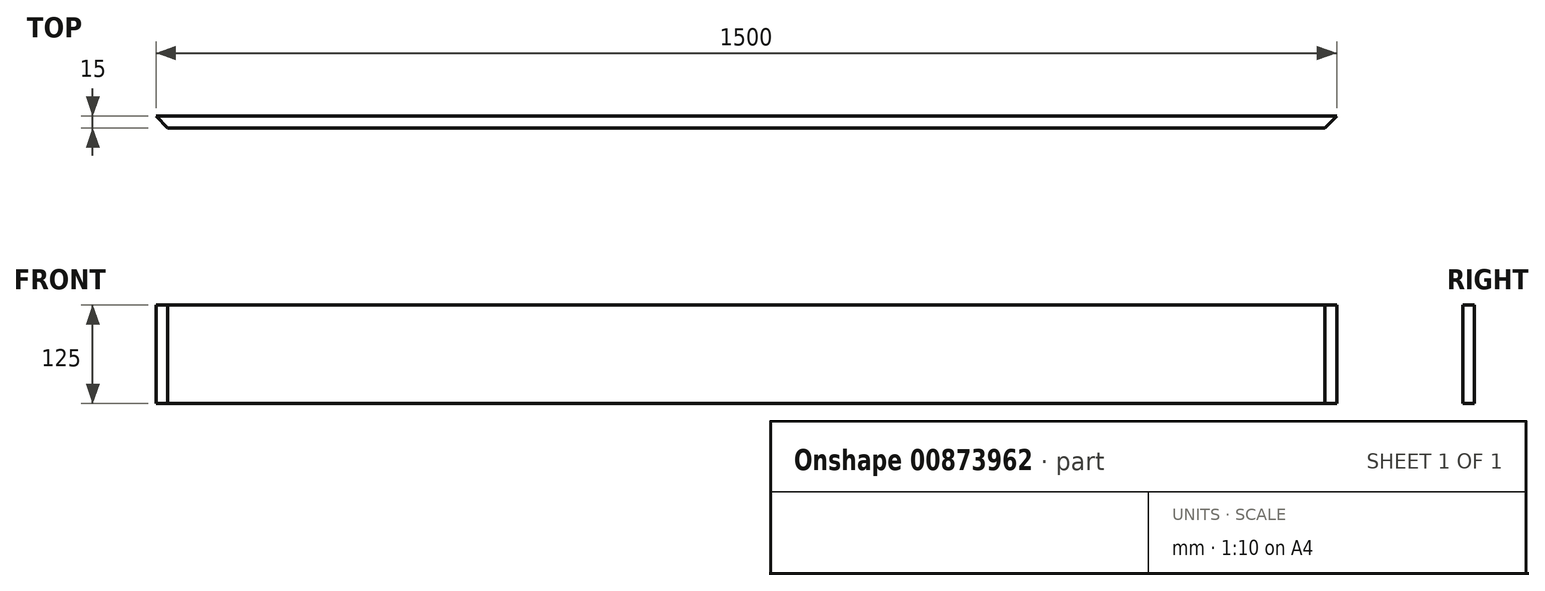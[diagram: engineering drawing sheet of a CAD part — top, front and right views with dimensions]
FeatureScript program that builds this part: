
annotation { "Feature Type Name" : "Feature", "Feature Type Description" : "" }
export const myFeature = defineFeature(function(context is Context, id is Id, definition is map)
    precondition{}
    {
        {
            var Q0;
            Q0=qCreatedBy(makeId("Front.planeOp"),FACE);
            var sketch = newSketch(context, id + "F0", { "sketchPlane" : qUnion([Q0])});
            skLineSegment(sketch, "E0.bottom", {"start": v(0, 0) * mm, "end": v(1500, 0) * mm});
            skLineSegment(sketch, "E0.top", {"start": v(0, 125) * mm, "end": v(1500, 125) * mm});
            skLineSegment(sketch, "E0.left", {"start": v(0, 0) * mm, "end": v(0, 125) * mm});
            skLineSegment(sketch, "E0.right", {"start": v(1500, 0) * mm, "end": v(1500, 125) * mm});
            skSolve(sketch);
        }
        {
            var Q0;
            Q0 = qSketchRegion(id + "F0", true);
            extrude(context, id + "F1", {"entities" : qUnion([Q0]), "depth" : 15 * mm, "offsetDistance" : 25 * mm});
        }
        {
            var Q0;
            Q0=makeQuery(id+"F1.opExtrude","SWEPT_FACE",FACE,{"disambiguationData":[OSD([sQuery(id+"F0.wireOp",EDGE,"E0.top")])]});
            var sketch = newSketch(context, id + "F2", { "sketchPlane" : qUnion([Q0])});
            skLineSegment(sketch, "E1", {"start": v(0, 0) * mm, "end": v(15, -15) * mm});
            skLineSegment(sketch, "E2", {"start": v(750, 0) * mm, "end": v(750, -15) * mm, "construction": true});
            skLineSegment(sketch, "E3.MirrorCS", {"start": v(1500, 0) * mm, "end": v(1485, -15) * mm});
            skSolve(sketch);
        }
        {
            var Q0;
            {var subQ0=sQuery(id+"F2.wireOp",EDGE,"E1");Q0=makeQuery(id+"F2.imprint","IMPRINT",FACE,{"disambiguationData":[TD([[makeQuery(id+"F2.imprint","IMPRINT",EDGE,{"derivedFrom":subQ0}),-1.0]])]});}
            var Q1;
            {var subQ0=sQuery(id+"F2.wireOp",EDGE,"E3.MirrorCS");Q1=makeQuery(id+"F2.imprint","IMPRINT",FACE,{"disambiguationData":[TD([[makeQuery(id+"F2.imprint","IMPRINT",EDGE,{"derivedFrom":subQ0}),1.0]])]});}
            extrude(context, id + "F3", {"entities" : qUnion([Q0, Q1]), "operationType" : NewBodyOperationType.REMOVE, "endBound" : BoundingType.THROUGH_ALL, "oppositeDirection" : true, "depth" : 25 * mm, "offsetDistance" : 25 * mm});
        }
    });
